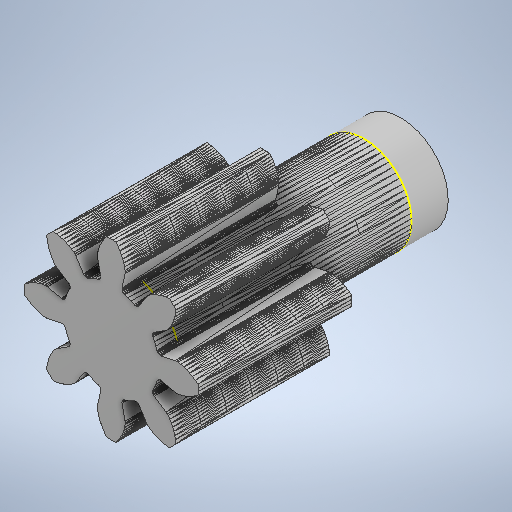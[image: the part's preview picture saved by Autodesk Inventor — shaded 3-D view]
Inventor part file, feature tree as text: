
AUTODESK INVENTOR PART (.ipt)
format: ipt  version: 2025.3 (Build 293356030, 356C)  size: 4,667,392 bytes
history: native  units: mm
features: other x3, sketch x2
ambient origin geometry x8: Origin, YZ Plane, XZ Plane, XY Plane, X Axis, Y Axis, Z Axis, Center Point
bodies: Solid1 (feature_tree)
feature tree (5):
  other  "encoder_shaft v1.ipt"
  other  "Solid1::encoder_shaft v1.ipt"
  other  "OperaciónIdentificador1"
  sketch  "Boceto1"  dims[d0=1.0mm]
  sketch  "Boceto2"
